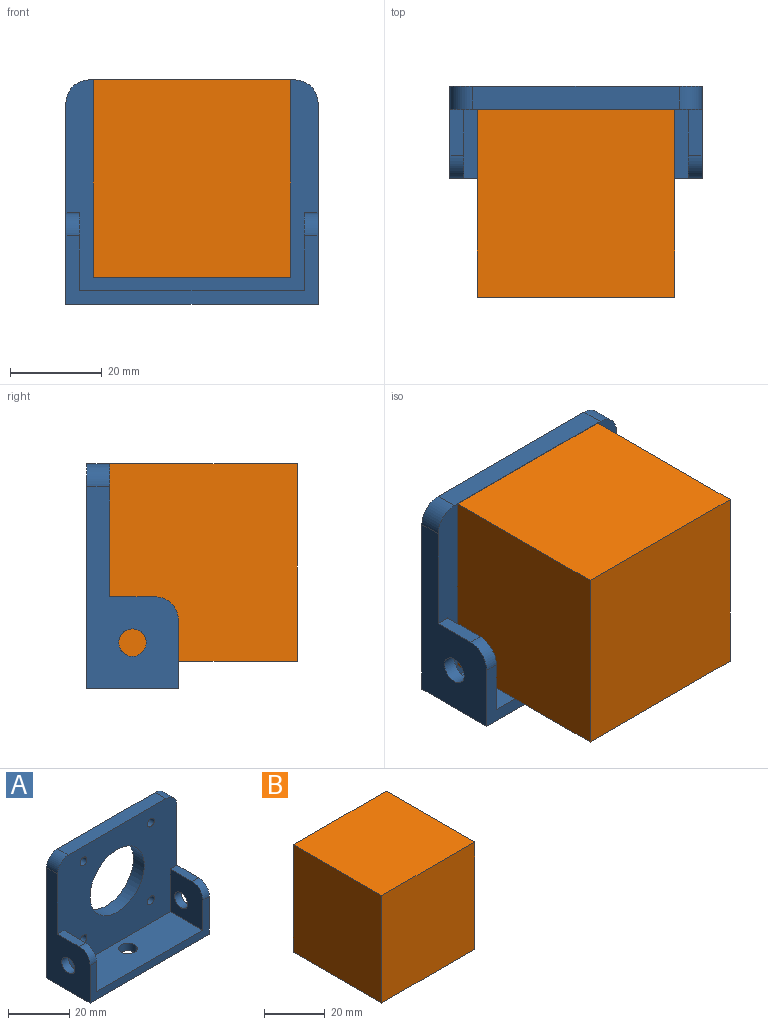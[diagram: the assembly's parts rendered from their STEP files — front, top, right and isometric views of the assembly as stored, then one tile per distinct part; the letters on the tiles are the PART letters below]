
ASSEMBLY  parts=2 mates=1
PART A: 32 faces, bbox 55x20x49 mm
  f0: plane 10x3mm, normal (0,0,1), area 30mm2, adj f4,f14,f15,f17
  f1: plane 55x20mm, normal (0,0,-1), area 1071.7mm2, adj f2,f3,f14,f26,f31
  f2: plane 55x15mm, normal (0,-1,0), area 237mm2, adj f1,f5,f14,f15,f17,f26,f27,f29
  f3: plane 55x49mm, normal (0,1,0), area 2080.3mm2, adj f1,f6,f7,f10,f13,f14,f16,f22
  f4: plane 55x46mm, normal (0,-1,0), area 1894.2mm2, adj f0,f5,f6,f7,f8,f11,f14,f15
  f5: plane 49x15mm, normal (0,0,1), area 706.7mm2, adj f2,f4,f15,f27,f31
  f6: plane 45x5mm, normal (0,0,1), area 225mm2, adj f3,f4,f16,f28
  f7: cylinder r=12.5mm len=25mm, axis (0,-1,0), area 392.7mm2, adj f3,f4
  f8: cylinder r=1.6mm len=3.2mm, axis (0,1,0), area 30.2mm2, adj f4,f9
  f9: plane 6x6mm, normal (0,1,0), area 20.2mm2, adj f8,f10
  f10: cylinder r=3mm len=6mm, axis (0,1,0), area 37.7mm2, adj f3,f9
  f11: cylinder r=1.6mm len=3.2mm, axis (0,1,0), area 30.2mm2, adj f4,f12
  f12: plane 6x6mm, normal (0,1,0), area 20.2mm2, adj f11,f13
  f13: cylinder r=3mm len=6mm, axis (0,1,0), area 37.7mm2, adj f3,f12
  f14: plane 44x20mm, normal (1,0,0), area 486.4mm2, adj f0,f1,f2,f3,f4,f16,f17,f18
  f15: plane 17x15mm, normal (-1,0,0), area 221.4mm2, adj f0,f2,f4,f5,f17,f18
  f16: cylinder r=5mm len=5mm, axis (0,1,0), area 39.3mm2, adj f3,f4,f6,f14
  f17: cylinder r=5mm len=5mm, axis (-1,0,0), area 23.6mm2, adj f0,f2,f14,f15
  f18: cylinder r=3mm len=6mm, axis (1,0,0), area 56.5mm2, adj f14,f15
  f19: plane 10x3mm, normal (0,0,1), area 30mm2, adj f4,f26,f27,f29
  f20: cylinder r=1.6mm len=3.2mm, axis (0,1,0), area 30.2mm2, adj f4,f21
  f21: plane 6x6mm, normal (0,1,0), area 20.2mm2, adj f20,f22
  f22: cylinder r=3mm len=6mm, axis (0,1,0), area 37.7mm2, adj f3,f21
  f23: cylinder r=1.6mm len=3.2mm, axis (0,1,0), area 30.2mm2, adj f4,f24
  f24: plane 6x6mm, normal (0,1,0), area 20.2mm2, adj f23,f25
  f25: cylinder r=3mm len=6mm, axis (0,1,0), area 37.7mm2, adj f3,f24
  f26: plane 44x20mm, normal (-1,0,0), area 486.4mm2, adj f1,f2,f3,f4,f19,f28,f29,f30
  f27: plane 17x15mm, normal (1,0,0), area 221.4mm2, adj f2,f4,f5,f19,f29,f30
  f28: cylinder r=5mm len=5mm, axis (0,1,0), area 39.3mm2, adj f3,f4,f6,f26
  f29: cylinder r=5mm len=5mm, axis (1,0,0), area 23.6mm2, adj f2,f19,f26,f27
  f30: cylinder r=3mm len=6mm, axis (-1,0,0), area 56.5mm2, adj f26,f27
  f31: cylinder r=3mm len=6mm, axis (0,0,-1), area 56.5mm2, adj f1,f5
PART B: 14 faces, bbox 43.2x41x43.2 mm
  f0: plane 43.2x41mm, normal (-1,0,0), area 1771.2mm2, adj f1,f3,f4,f5
  f1: plane 43.2x41mm, normal (0,0,-1), area 1771.2mm2, adj f0,f2,f4,f5
  f2: plane 43.2x41mm, normal (1,0,0), area 1771.2mm2, adj f1,f3,f4,f5
  f3: plane 43.2x41mm, normal (0,0,1), area 1771.2mm2, adj f0,f2,f4,f5
  f4: plane 43.2x43.2mm, normal (0,-1,0), area 1866.2mm2, adj f0,f1,f2,f3
  f5: plane 43.2x43.2mm, normal (0,1,0), area 1838mm2, adj f0,f1,f2,f3,f6,f8,f10,f12
  f6: cylinder r=1.5mm len=15mm, axis (0,1,0), area 141.4mm2, adj f5,f7
  f7: cone r=0mm half-angle=59deg, axis (0,1,0), area 8.2mm2, adj f6
  f8: cylinder r=1.5mm len=15mm, axis (0,1,0), area 141.4mm2, adj f5,f9
  f9: cone r=0mm half-angle=59deg, axis (0,1,0), area 8.2mm2, adj f8
  f10: cylinder r=1.5mm len=15mm, axis (0,1,0), area 141.4mm2, adj f5,f11
  f11: cone r=0mm half-angle=59deg, axis (0,1,0), area 8.2mm2, adj f10
  f12: cylinder r=1.5mm len=15mm, axis (0,1,0), area 141.4mm2, adj f5,f13
  f13: cone r=0mm half-angle=59deg, axis (0,1,0), area 8.2mm2, adj f12
PLACE A at identity
PLACE B t=(-21.6,0,21.6)mm
MATE fastened B.f6 <-> A.f8  axis (0,1,0) through (15.5,0,15.5)mm
